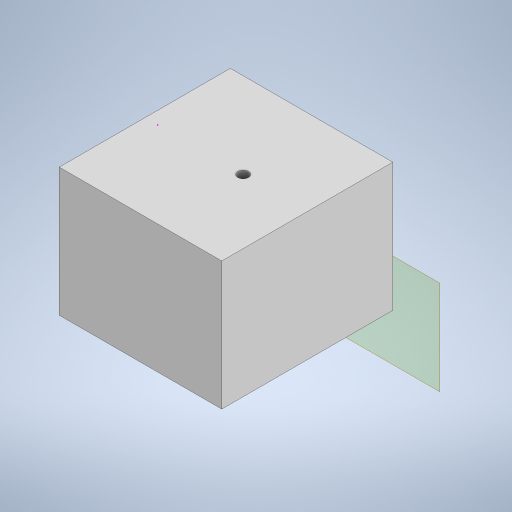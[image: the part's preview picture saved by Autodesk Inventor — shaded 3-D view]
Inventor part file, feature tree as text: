
AUTODESK INVENTOR PART (.ipt)
format: ipt  version: 2023 (Build 270158000, 158)  size: 260,096 bytes
history: native  units: mm
features: sketch x7, plane x6, extrude x5
ambient origin geometry x8: Origin, YZ Plane, XZ Plane, XY Plane, X Axis, Y Axis, Z Axis, Center Point
bodies: Body1 (feature_tree)
feature tree (18):
  plane  "Work Plane13"
  extrude  "Extrusion34"  Depth=40.0mm
  sketch  "Sketch46"  dims[d144=30.0mm d145=0.0mm d146=36.0mm]
  plane  "Work Plane11"
  extrude  "Extrusion35"  Depth=36.0mm
  sketch  "Sketch48"  dims[d150=0.0mm d151=0.0mm d156=20.0mm]
  extrude  "Extrusion36"  Depth=2.5mm
  plane  "Work Plane7"
  extrude  "Extrusion38"  Depth=20.0mm
  plane  "Work Plane4"
  extrude  "Extrusion39"  Depth=15.0mm TaperAngle=0.0deg
  plane  "Work Plane1"
  plane  "Work Plane6"
  sketch  "Sketch45"  dims[d142=38.0mm d143=40.0mm]
  sketch  "Sketch47"  dims[d147=30.0mm d148=-2.617994mm d149=2.5mm]
  sketch  "Sketch49"  dims[d157=15.0mm d158=15.0mm d159=0.0mm]
  sketch  "Sketch58"  dims[d160=4.0mm]
  sketch  "Sketch59"  dims[d161=20.0mm d162=35.0mm d163=0.0mm d49=0.5mm d50=0.872665mm d51=0.5mm d52=0.872665mm d130=0.5mm d131=0.872665mm d132=0.5mm d133=0.872665mm]
